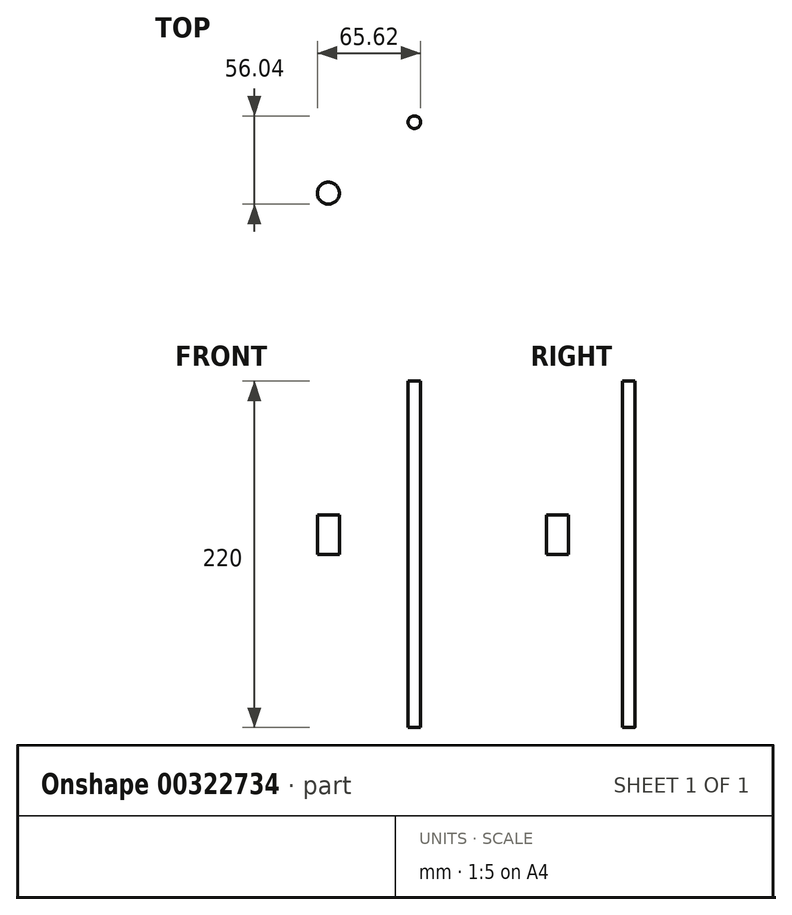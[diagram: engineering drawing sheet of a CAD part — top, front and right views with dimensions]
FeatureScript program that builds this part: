
annotation { "Feature Type Name" : "Feature", "Feature Type Description" : "" }
export const myFeature = defineFeature(function(context is Context, id is Id, definition is map)
    precondition{}
    {
        {
            var Q0;
            Q0=qCreatedBy(makeId("Top.planeOp"),FACE);
            var sketch = newSketch(context, id + "F0", { "sketchPlane" : qUnion([Q0])});
            skCircle(sketch, "E0", {"center": v(0, 0) * mm, "radius": 4 * mm});
            skSolve(sketch);
        }
        {
            var Q0;
            Q0=makeQuery(id+"F0.imprint","IMPRINT",FACE,{"disambiguationData":[TD([[makeQuery(id+"F0.imprint","IMPRINT",EDGE,{"derivedFrom":sQuery(id+"F0.wireOp",EDGE,"E0")}),1.0]])]});
            extrude(context, id + "F1", {"entities" : qUnion([Q0]), "depth" : 220 * mm, "symmetric" : true});
        }
        {
            var Q0;
            Q0=qCreatedBy(makeId("Top.planeOp"),FACE);
            var sketch = newSketch(context, id + "F2", { "sketchPlane" : qUnion([Q0])});
            skCircle(sketch, "E1", {"center": v(-54.62, -45.04) * mm, "radius": 7 * mm});
            skSolve(sketch);
        }
        {
            var Q0;
            Q0=makeQuery(id+"F2.imprint","IMPRINT",FACE,{"disambiguationData":[TD([[makeQuery(id+"F2.imprint","IMPRINT",EDGE,{"derivedFrom":sQuery(id+"F2.wireOp",EDGE,"E1")}),1.0]])]});
            extrude(context, id + "F3", {"entities" : qUnion([Q0]), "depth" : 25 * mm, "offsetDistance" : 25 * mm});
        }
    });
